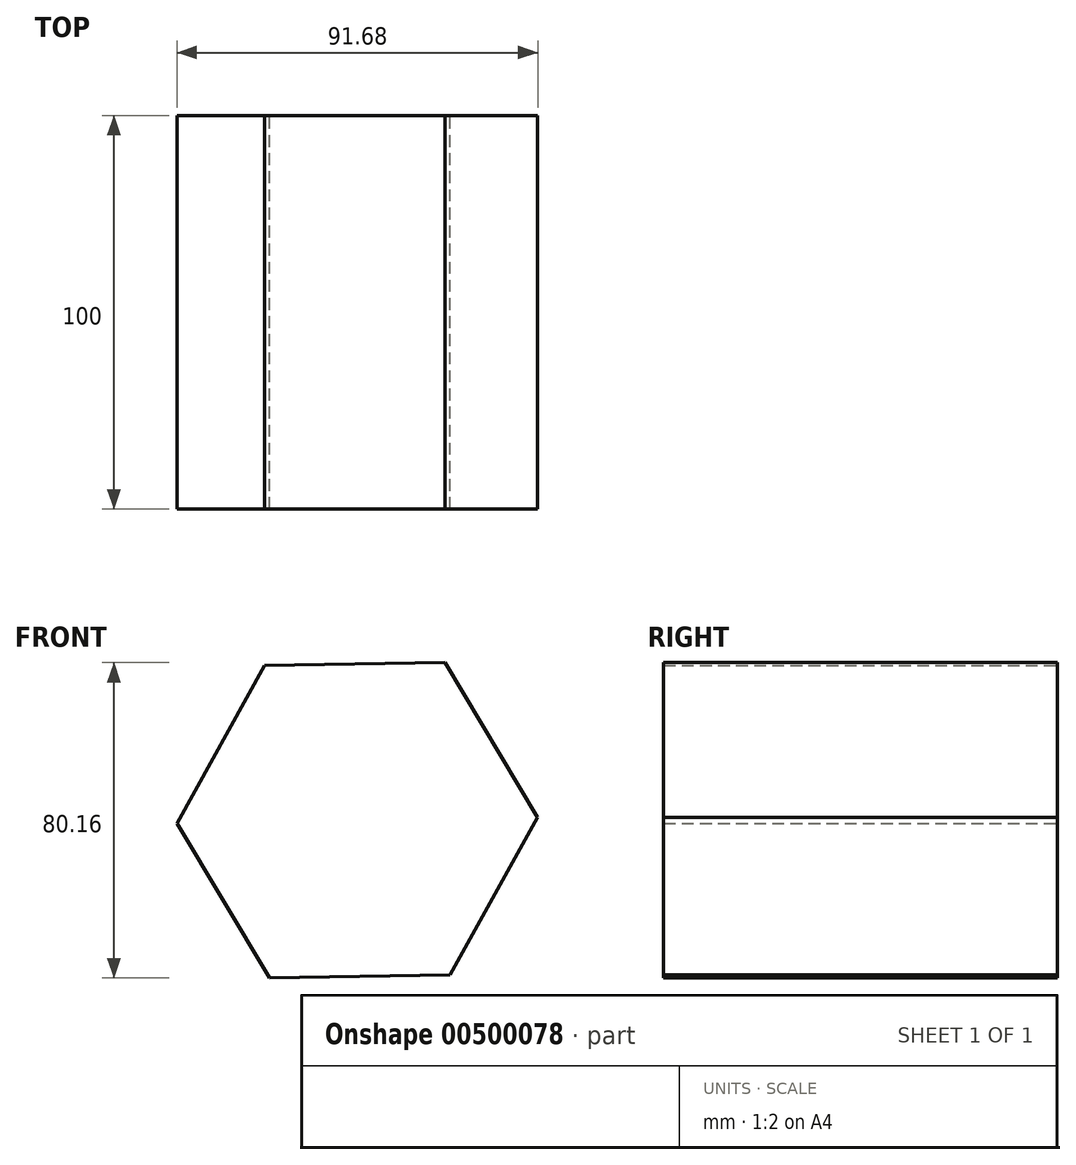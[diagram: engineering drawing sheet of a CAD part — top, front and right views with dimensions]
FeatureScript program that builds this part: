
annotation { "Feature Type Name" : "Feature", "Feature Type Description" : "" }
export const myFeature = defineFeature(function(context is Context, id is Id, definition is map)
    precondition{}
    {
        {
            var Q0;
            Q0=qCreatedBy(makeId("Front.planeOp"),FACE);
            var sketch = newSketch(context, id + "F0", { "sketchPlane" : qUnion([Q0])});
            skCircle(sketch, "E0.cCircle", {"center": v(0, 0) * mm, "radius": 45.84 * mm, "construction": true});
            skLineSegment(sketch, "E0.0", {"start": v(22.25, 40.08) * mm, "end": v(45.84, 0.77) * mm});
            skLineSegment(sketch, "E0.1", {"start": v(45.84, 0.77) * mm, "end": v(23.59, -39.31) * mm});
            skLineSegment(sketch, "E0.2", {"start": v(23.59, -39.31) * mm, "end": v(-22.25, -40.08) * mm});
            skLineSegment(sketch, "E0.3", {"start": v(-22.25, -40.08) * mm, "end": v(-45.84, -0.77) * mm});
            skLineSegment(sketch, "E0.4", {"start": v(-45.84, -0.77) * mm, "end": v(-23.59, 39.31) * mm});
            skLineSegment(sketch, "E0.5", {"start": v(-23.59, 39.31) * mm, "end": v(22.25, 40.08) * mm});
            skSolve(sketch);
        }
        {
            var Q0;
            Q0=makeQuery(id+"F0.imprint","IMPRINT",FACE,{"disambiguationData":[TD([[makeQuery(id+"F0.imprint","IMPRINT",EDGE,{"derivedFrom":sQuery(id+"F0.wireOp",EDGE,"E0.0")}),-1.0]])]});
            extrude(context, id + "F1", {"entities" : qUnion([Q0]), "endBound" : BoundingType.SYMMETRIC, "depth" : 100 * mm});
        }
    });
